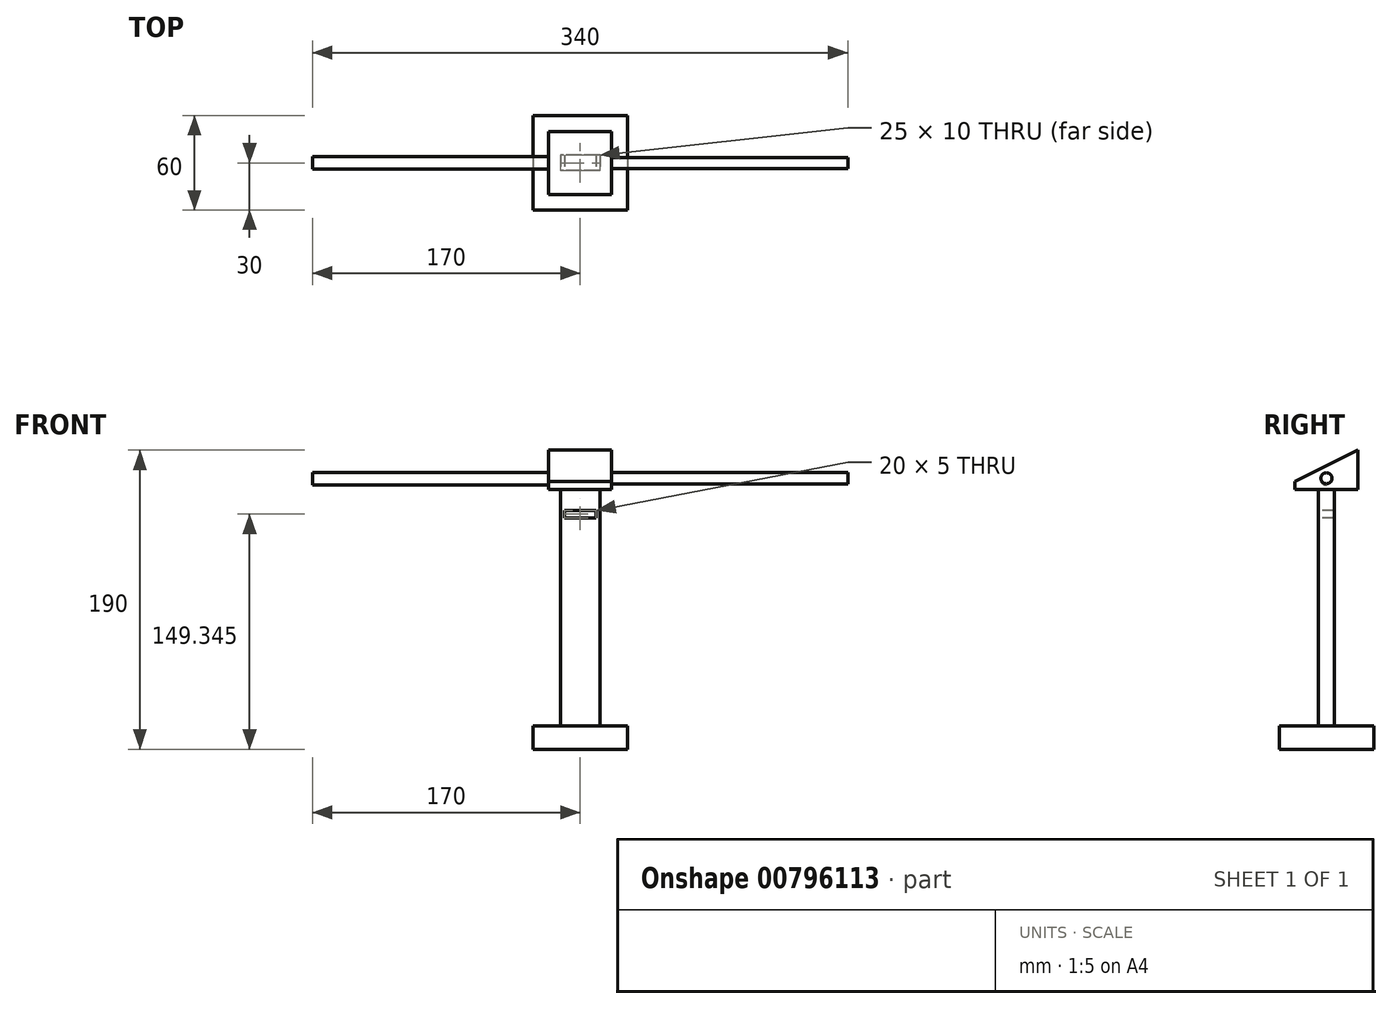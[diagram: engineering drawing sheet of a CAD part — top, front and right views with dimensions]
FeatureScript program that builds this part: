
annotation { "Feature Type Name" : "Feature", "Feature Type Description" : "" }
export const myFeature = defineFeature(function(context is Context, id is Id, definition is map)
    precondition{}
    {
        {
            var Q0;
            Q0=qCreatedBy(makeId("Top.planeOp"),FACE);
            var sketch = newSketch(context, id + "F0", { "sketchPlane" : qUnion([Q0])});
            skLineSegment(sketch, "E0.bottom", {"start": v(30, 30) * mm, "end": v(-30, 30) * mm});
            skLineSegment(sketch, "E0.top", {"start": v(30, -30) * mm, "end": v(-30, -30) * mm});
            skLineSegment(sketch, "E0.left", {"start": v(30, 30) * mm, "end": v(30, -30) * mm});
            skLineSegment(sketch, "E0.right", {"start": v(-30, 30) * mm, "end": v(-30, -30) * mm});
            skPoint(sketch, "E0.middle", {"position": v(0, 0) * mm});
            skSolve(sketch);
        }
        {
            var Q0;
            Q0=makeQuery(id+"F0.imprint","IMPRINT",FACE,{"disambiguationData":[TD([[makeQuery(id+"F0.imprint","IMPRINT",EDGE,{"derivedFrom":sQuery(id+"F0.wireOp",EDGE,"E0.bottom")}),1.0]])]});
            extrude(context, id + "F1", {"entities" : qUnion([Q0]), "depth" : 15 * mm, "offsetDistance" : 25 * mm});
        }
        {
            var Q0;
            Q0=makeQuery(id+"F1.opExtrude","CAP_FACE",FACE,{"disambiguationData":[OSD([sQuery(id+"F0.wireOp",EDGE,"E0.bottom"),sQuery(id+"F0.wireOp",EDGE,"E0.top"),sQuery(id+"F0.wireOp",EDGE,"E0.left"),sQuery(id+"F0.wireOp",EDGE,"E0.right")])],"isStart":false});
            var sketch = newSketch(context, id + "F2", { "sketchPlane" : qUnion([Q0])});
            skLineSegment(sketch, "E1.bottom", {"start": v(12.5, 5) * mm, "end": v(-12.5, 5) * mm});
            skLineSegment(sketch, "E1.top", {"start": v(12.5, -5) * mm, "end": v(-12.5, -5) * mm});
            skLineSegment(sketch, "E1.left", {"start": v(12.5, 5) * mm, "end": v(12.5, -5) * mm});
            skLineSegment(sketch, "E1.right", {"start": v(-12.5, 5) * mm, "end": v(-12.5, -5) * mm});
            skPoint(sketch, "E1.middle", {"position": v(0, 0) * mm});
            skSolve(sketch);
        }
        {
            var Q0;
            Q0=makeQuery(id+"F2.imprint","IMPRINT",FACE,{"disambiguationData":[TD([[makeQuery(id+"F2.imprint","IMPRINT",EDGE,{"derivedFrom":sQuery(id+"F2.wireOp",EDGE,"E1.bottom")}),1.0]])]});
            extrude(context, id + "F3", {"entities" : qUnion([Q0]), "operationType" : NewBodyOperationType.ADD, "depth" : 150 * mm, "offsetDistance" : 25 * mm});
        }
        {
            var Q0;
            Q0=makeQuery(id+"F3.opExtrude","CAP_FACE",FACE,{"disambiguationData":[OSD([sQuery(id+"F2.wireOp",EDGE,"E1.bottom"),sQuery(id+"F2.wireOp",EDGE,"E1.top"),sQuery(id+"F2.wireOp",EDGE,"E1.left"),sQuery(id+"F2.wireOp",EDGE,"E1.right")])],"isStart":false});
            var sketch = newSketch(context, id + "F4", { "sketchPlane" : qUnion([Q0])});
            skLineSegment(sketch, "E2.bottom", {"start": v(20, 20) * mm, "end": v(-20, 20) * mm});
            skLineSegment(sketch, "E2.top", {"start": v(20, -20) * mm, "end": v(-20, -20) * mm});
            skLineSegment(sketch, "E2.left", {"start": v(20, 20) * mm, "end": v(20, -20) * mm});
            skLineSegment(sketch, "E2.right", {"start": v(-20, 20) * mm, "end": v(-20, -20) * mm});
            skPoint(sketch, "E2.middle", {"position": v(0, 0) * mm});
            skSolve(sketch);
        }
        {
            var Q0;
            Q0=makeQuery(id+"F4.imprint","IMPRINT",FACE,{"disambiguationData":[TD([[makeQuery(id+"F4.imprint","IMPRINT",EDGE,{"derivedFrom":makeQuery(id+"F3.opExtrude","CAP_EDGE",EDGE,{"disambiguationData":[OSD([sQuery(id+"F2.wireOp",EDGE,"E1.bottom")])],"isStart":false})}),1.0]])]});
            var Q1;
            Q1=makeQuery(id+"F4.imprint","IMPRINT",FACE,{"disambiguationData":[TD([[makeQuery(id+"F4.imprint","IMPRINT",EDGE,{"derivedFrom":sQuery(id+"F4.wireOp",EDGE,"E2.bottom")}),1.0]])]});
            extrude(context, id + "F5", {"entities" : qUnion([Q0, Q1]), "operationType" : NewBodyOperationType.ADD, "depth" : 25 * mm, "offsetDistance" : 25 * mm});
        }
        {
            var Q0;
            Q0=makeQuery(id+"F5.opExtrude","CAP_EDGE",EDGE,{"disambiguationData":[OSD([sQuery(id+"F4.wireOp",EDGE,"E2.top")])],"isStart":false});
            chamfer(context, id + "F6", {"entities" : qUnion([Q0]), "chamferType" : ChamferType.TWO_OFFSETS, "width1" : 20 * mm, "oppositeDirection" : false, "width2" : 40 * mm, "tangentPropagation" : true});
        }
        {
            var Q0;
            Q0=makeQuery(id+"F3.opExtrude","SWEPT_FACE",FACE,{"disambiguationData":[OSD([sQuery(id+"F2.wireOp",EDGE,"E1.top")])]});
            var sketch = newSketch(context, id + "F7", { "sketchPlane" : qUnion([Q0])});
            skLineSegment(sketch, "E3.bottom", {"start": v(10, 151.84) * mm, "end": v(-10, 151.84) * mm});
            skLineSegment(sketch, "E3.top", {"start": v(10, 146.84) * mm, "end": v(-10, 146.84) * mm});
            skLineSegment(sketch, "E3.left", {"start": v(10, 151.84) * mm, "end": v(10, 146.84) * mm});
            skLineSegment(sketch, "E3.right", {"start": v(-10, 151.84) * mm, "end": v(-10, 146.84) * mm});
            skPoint(sketch, "E3.middle", {"position": v(0, 149.34) * mm});
            skPoint(sketch, "E3.middle.positionSnap0", {"position": v(0, 165) * mm});
            skPoint(sketch, "E3.centerSnap0", {"position": v(0, 165) * mm});
            skSolve(sketch);
        }
        {
            var Q0;
            Q0=makeQuery(id+"F7.imprint","IMPRINT",FACE,{"disambiguationData":[TD([[makeQuery(id+"F7.imprint","IMPRINT",EDGE,{"derivedFrom":sQuery(id+"F7.wireOp",EDGE,"E3.bottom")}),1.0]])]});
            extrude(context, id + "F8", {"entities" : qUnion([Q0]), "operationType" : NewBodyOperationType.REMOVE, "oppositeDirection" : true, "depth" : 25 * mm, "offsetDistance" : 25 * mm});
        }
        {
            var Q0;
            Q0=makeQuery(id+"F5.opExtrude","SWEPT_FACE",FACE,{"disambiguationData":[OSD([sQuery(id+"F4.wireOp",EDGE,"E2.left")])]});
            var sketch = newSketch(context, id + "F9", { "sketchPlane" : qUnion([Q0])});
            skCircle(sketch, "E4", {"center": v(0, 172.18) * mm, "radius": 3.5 * mm});
            skSolve(sketch);
        }
        {
            var Q0;
            Q0=makeQuery(id+"F9.imprint","IMPRINT",FACE,{"disambiguationData":[TD([[makeQuery(id+"F9.imprint","IMPRINT",EDGE,{"derivedFrom":sQuery(id+"F9.wireOp",EDGE,"E4")}),1.0]])]});
            extrude(context, id + "F10", {"entities" : qUnion([Q0]), "operationType" : NewBodyOperationType.ADD, "depth" : 150 * mm, "offsetDistance" : 25 * mm});
        }
        {
            var Q0;
            Q0=makeQuery(id+"F5.opExtrude","SWEPT_FACE",FACE,{"disambiguationData":[OSD([sQuery(id+"F4.wireOp",EDGE,"E2.right")])]});
            var sketch = newSketch(context, id + "F11", { "sketchPlane" : qUnion([Q0])});
            skCircle(sketch, "E5", {"center": v(0, 171.85) * mm, "radius": 4 * mm});
            skSolve(sketch);
        }
        {
            var Q0;
            Q0=makeQuery(id+"F11.imprint","IMPRINT",FACE,{"disambiguationData":[TD([[makeQuery(id+"F11.imprint","IMPRINT",EDGE,{"derivedFrom":sQuery(id+"F11.wireOp",EDGE,"E5")}),1.0]])]});
            extrude(context, id + "F12", {"entities" : qUnion([Q0]), "operationType" : NewBodyOperationType.ADD, "depth" : 150 * mm, "offsetDistance" : 25 * mm});
        }
    });
